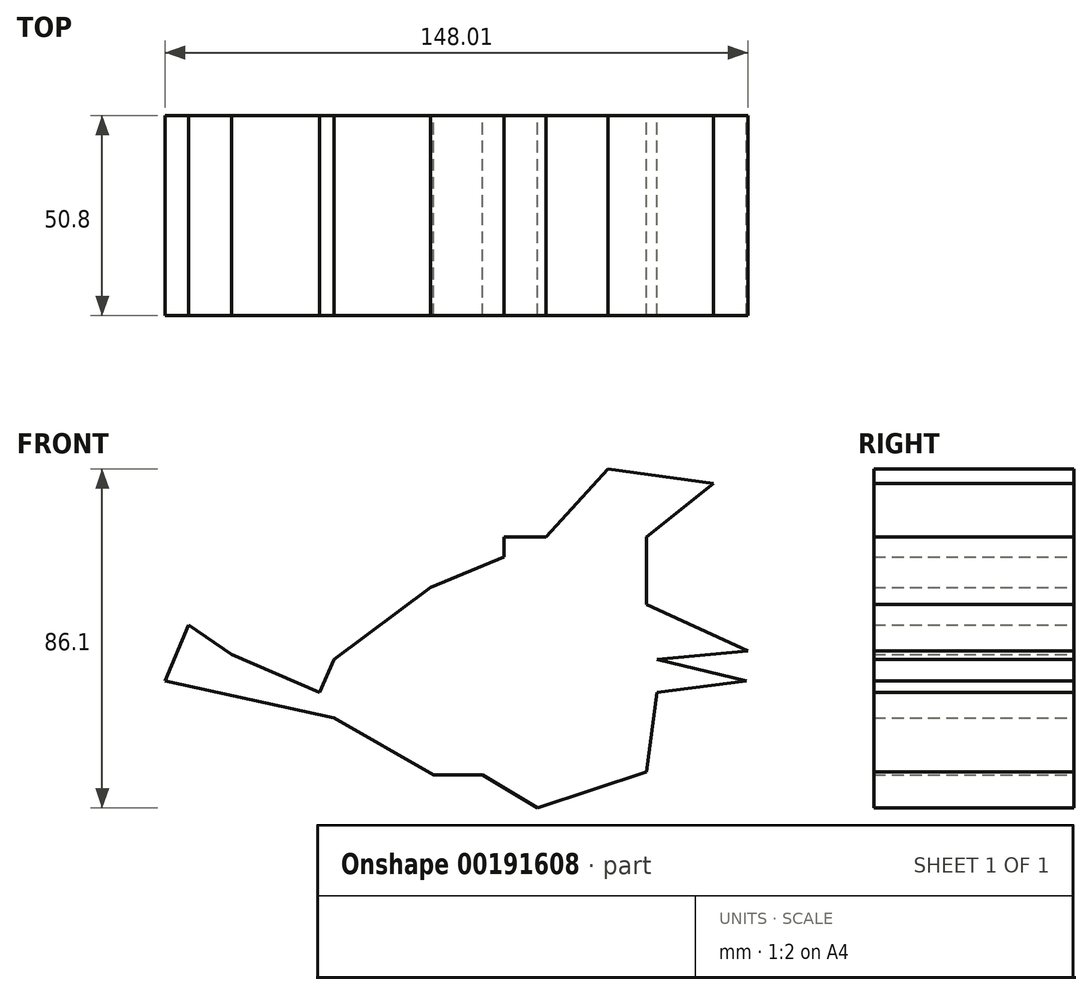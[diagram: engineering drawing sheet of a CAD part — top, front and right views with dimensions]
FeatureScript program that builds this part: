
annotation { "Feature Type Name" : "Feature", "Feature Type Description" : "" }
export const myFeature = defineFeature(function(context is Context, id is Id, definition is map)
    precondition{}
    {
        {
            var Q0;
            Q0=qCreatedBy(makeId("Front.planeOp"),FACE);
            var sketch = newSketch(context, id + "F0", { "sketchPlane" : qUnion([Q0])});
            skLineSegment(sketch, "E0", {"start": v(25.77, 17.05) * mm, "end": v(0, 28.78) * mm});
            skLineSegment(sketch, "E1", {"start": v(0, 28.78) * mm, "end": v(0, 46) * mm});
            skLineSegment(sketch, "E2", {"start": v(0, 46) * mm, "end": v(16.98, 59.55) * mm});
            skLineSegment(sketch, "E3", {"start": v(16.98, 59.55) * mm, "end": v(-9.77, 63.22) * mm});
            skLineSegment(sketch, "E4", {"start": v(-9.77, 63.22) * mm, "end": v(-25.52, 46) * mm});
            skLineSegment(sketch, "E5", {"start": v(-25.52, 46) * mm, "end": v(-36.14, 46) * mm});
            skLineSegment(sketch, "E6", {"start": v(-36.14, 46) * mm, "end": v(-36.14, 40.87) * mm});
            skLineSegment(sketch, "E7", {"start": v(-36.14, 40.87) * mm, "end": v(-54.83, 33.17) * mm});
            skLineSegment(sketch, "E8", {"start": v(-54.83, 33.17) * mm, "end": v(-79.37, 14.86) * mm});
            skLineSegment(sketch, "E9", {"start": v(-79.37, 14.86) * mm, "end": v(-83.04, 6.43) * mm});
            skLineSegment(sketch, "E10", {"start": v(-83.04, 6.43) * mm, "end": v(-105.33, 16.12) * mm});
            skLineSegment(sketch, "E11", {"start": v(-105.33, 16.12) * mm, "end": v(-116.38, 23.65) * mm});
            skLineSegment(sketch, "E12", {"start": v(-116.38, 23.65) * mm, "end": v(-122.24, 9.36) * mm});
            skLineSegment(sketch, "E13", {"start": v(-122.24, 9.36) * mm, "end": v(-79.37, 0) * mm});
            skLineSegment(sketch, "E14", {"start": v(-79.37, 0) * mm, "end": v(-54.1, -14.45) * mm});
            skLineSegment(sketch, "E15", {"start": v(-54.1, -14.45) * mm, "end": v(-41.64, -14.45) * mm});
            skLineSegment(sketch, "E16", {"start": v(-41.64, -14.45) * mm, "end": v(-27.72, -22.88) * mm});
            skLineSegment(sketch, "E17", {"start": v(-27.72, -22.88) * mm, "end": v(0, -13.72) * mm});
            skLineSegment(sketch, "E18", {"start": v(0, -13.72) * mm, "end": v(2.7, 6.43) * mm});
            skLineSegment(sketch, "E19", {"start": v(2.7, 6.43) * mm, "end": v(25.4, 9.36) * mm});
            skLineSegment(sketch, "E20", {"start": v(25.4, 9.36) * mm, "end": v(2.7, 14.86) * mm});
            skLineSegment(sketch, "E21", {"start": v(2.7, 14.86) * mm, "end": v(25.77, 17.05) * mm});
            skSolve(sketch);
        }
        {
            var Q0;
            Q0=makeQuery(id+"F0.imprint","IMPRINT",FACE,{"disambiguationData":[TD([[makeQuery(id+"F0.imprint","IMPRINT",EDGE,{"derivedFrom":sQuery(id+"F0.wireOp",EDGE,"E0")}),1.0]])]});
            extrude(context, id + "F1", {"entities" : qUnion([Q0]), "depth" : 50.8 * mm});
        }
    });
